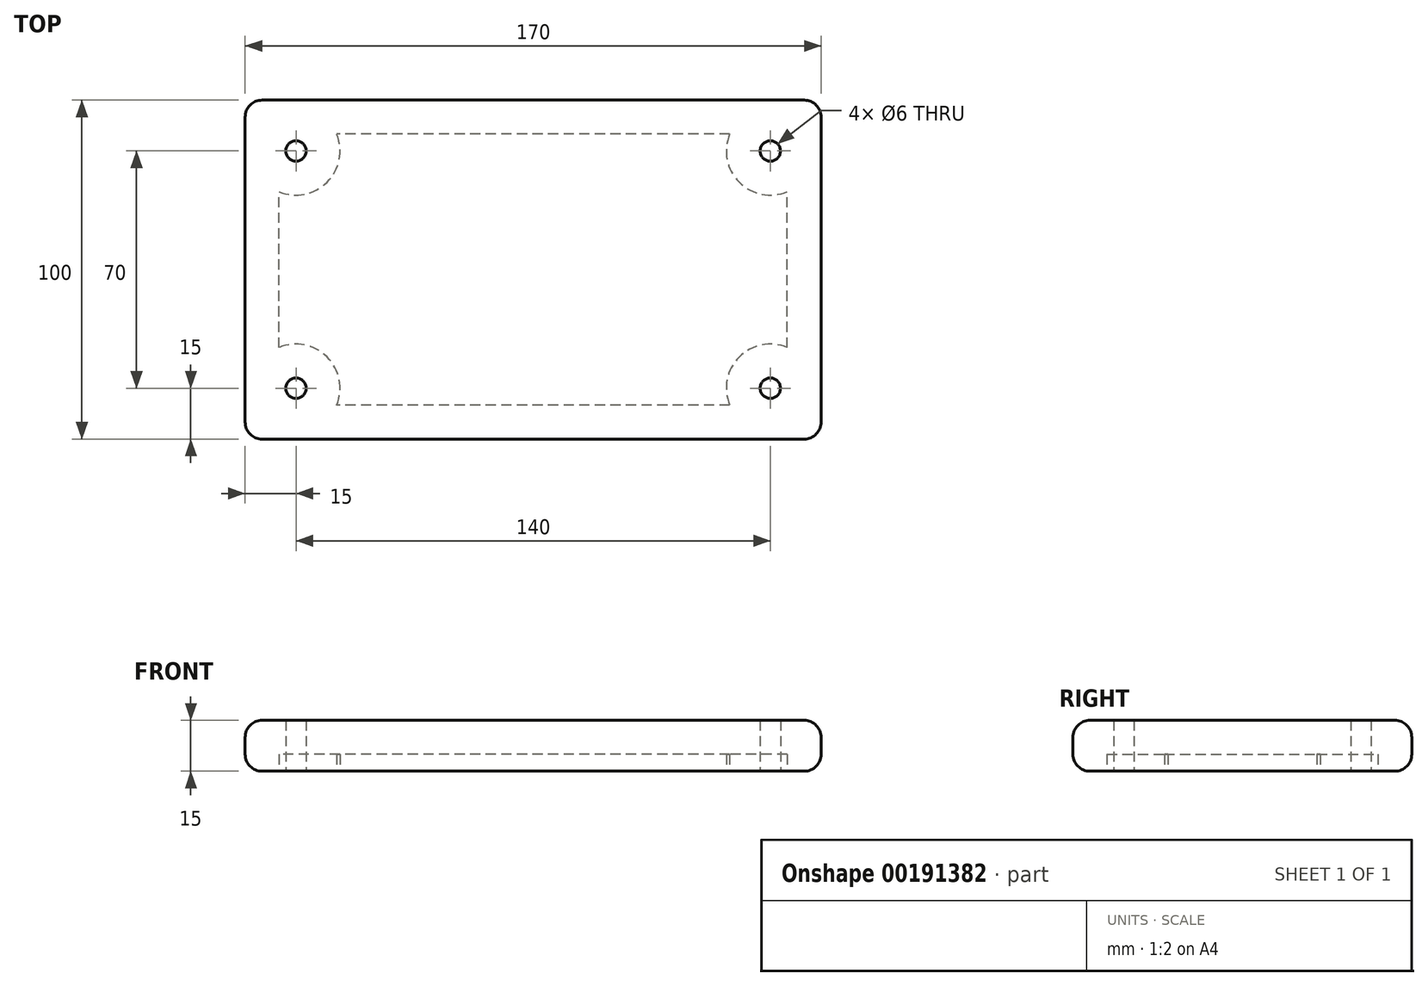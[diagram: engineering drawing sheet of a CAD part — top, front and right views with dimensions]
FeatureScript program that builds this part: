
annotation { "Feature Type Name" : "Feature", "Feature Type Description" : "" }
export const myFeature = defineFeature(function(context is Context, id is Id, definition is map)
    precondition{}
    {
        {
            var Q0;
            Q0=qCreatedBy(makeId("Top.planeOp"),FACE);
            var sketch = newSketch(context, id + "F0", { "sketchPlane" : qUnion([Q0])});
            skLineSegment(sketch, "E0.bottom", {"start": v(85, -50) * mm, "end": v(-85, -50) * mm});
            skLineSegment(sketch, "E0.top", {"start": v(85, 50) * mm, "end": v(-85, 50) * mm});
            skLineSegment(sketch, "E0.left", {"start": v(85, -50) * mm, "end": v(85, 50) * mm});
            skLineSegment(sketch, "E0.right", {"start": v(-85, -50) * mm, "end": v(-85, 50) * mm});
            skPoint(sketch, "E0.middle", {"position": v(0, 0) * mm});
            skCircle(sketch, "E1", {"center": v(-70, -35) * mm, "radius": 3 * mm});
            skCircle(sketch, "E2", {"center": v(-70, 35) * mm, "radius": 3 * mm});
            skCircle(sketch, "E3", {"center": v(70, -35) * mm, "radius": 3 * mm});
            skCircle(sketch, "E4", {"center": v(70, 35) * mm, "radius": 3 * mm});
            skSolve(sketch);
        }
        {
            var Q0;
            Q0=makeQuery(id+"F0.imprint","IMPRINT",FACE,{"disambiguationData":[TD([[makeQuery(id+"F0.imprint","IMPRINT",EDGE,{"derivedFrom":sQuery(id+"F0.wireOp",EDGE,"E0.bottom")}),-1.0]])]});
            extrude(context, id + "F1", {"entities" : qUnion([Q0]), "endBound" : BoundingType.SYMMETRIC, "depth" : 15 * mm});
        }
        {
            var Q0;
            Q0=makeQuery(id+"F1.opExtrude","CAP_FACE",FACE,{"disambiguationData":[OSD([sQuery(id+"F0.wireOp",EDGE,"E0.bottom"),sQuery(id+"F0.wireOp",EDGE,"E0.top"),sQuery(id+"F0.wireOp",EDGE,"E0.left"),sQuery(id+"F0.wireOp",EDGE,"E0.right")])],"isStart":true});
            shell(context, id + "F2", {"entities" : qUnion([Q0]), "thickness" : 10 * mm});
        }
        {
            var Q0;
            Q0=makeQuery(id+"F1.opExtrude","CAP_EDGE",EDGE,{"disambiguationData":[OSD([sQuery(id+"F0.wireOp",EDGE,"E0.right")])],"isStart":true});
            var Q1;
            Q1=makeQuery(id+"F1.opExtrude","CAP_EDGE",EDGE,{"disambiguationData":[OSD([sQuery(id+"F0.wireOp",EDGE,"E0.right")])],"isStart":false});
            var Q2;
            Q2=makeQuery(id+"F1.opExtrude","CAP_EDGE",EDGE,{"disambiguationData":[OSD([sQuery(id+"F0.wireOp",EDGE,"E0.bottom")])],"isStart":false});
            var Q3;
            Q3=makeQuery(id+"F1.opExtrude","CAP_EDGE",EDGE,{"disambiguationData":[OSD([sQuery(id+"F0.wireOp",EDGE,"E0.bottom")])],"isStart":true});
            var Q4;
            Q4=makeQuery(id+"F1.opExtrude","CAP_EDGE",EDGE,{"disambiguationData":[OSD([sQuery(id+"F0.wireOp",EDGE,"E0.left")])],"isStart":true});
            var Q5;
            Q5=makeQuery(id+"F1.opExtrude","CAP_EDGE",EDGE,{"disambiguationData":[OSD([sQuery(id+"F0.wireOp",EDGE,"E0.left")])],"isStart":false});
            var Q6;
            Q6=makeQuery(id+"F1.opExtrude","SWEPT_EDGE",EDGE,{"disambiguationData":[OSD([sQuery(id+"F0.wireOp",EDGE,"E0.top"),sQuery(id+"F0.wireOp",EDGE,"E0.left")])]});
            var Q7;
            Q7=makeQuery(id+"F1.opExtrude","CAP_EDGE",EDGE,{"disambiguationData":[OSD([sQuery(id+"F0.wireOp",EDGE,"E0.top")])],"isStart":false});
            var Q8;
            Q8=makeQuery(id+"F1.opExtrude","CAP_EDGE",EDGE,{"disambiguationData":[OSD([sQuery(id+"F0.wireOp",EDGE,"E0.top")])],"isStart":true});
            var Q9;
            Q9=makeQuery(id+"F1.opExtrude","SWEPT_EDGE",EDGE,{"disambiguationData":[OSD([sQuery(id+"F0.wireOp",EDGE,"E0.top"),sQuery(id+"F0.wireOp",EDGE,"E0.right")])]});
            var Q10;
            Q10=makeQuery(id+"F1.opExtrude","SWEPT_EDGE",EDGE,{"disambiguationData":[OSD([sQuery(id+"F0.wireOp",EDGE,"E0.bottom"),sQuery(id+"F0.wireOp",EDGE,"E0.right")])]});
            var Q11;
            Q11=makeQuery(id+"F1.opExtrude","SWEPT_EDGE",EDGE,{"disambiguationData":[OSD([sQuery(id+"F0.wireOp",EDGE,"E0.bottom"),sQuery(id+"F0.wireOp",EDGE,"E0.left")])]});
            fillet(context, id + "F3", {"entities" : qUnion([Q0, Q1, Q2, Q3, Q4, Q5, Q6, Q7, Q8, Q9, Q10, Q11]), "radius" : 5 * mm, "tangentPropagation" : true, "allowEdgeOverflow" : false});
        }
        {
            var Q0;
            Q0=makeQuery(id+"F2.opShell","OFFSET_FACE",FACE,{"disambiguationData":[OSD([sQuery(id+"F0.wireOp",EDGE,"E0.bottom"),sQuery(id+"F0.wireOp",EDGE,"E0.top"),sQuery(id+"F0.wireOp",EDGE,"E0.left"),sQuery(id+"F0.wireOp",EDGE,"E0.right")])]});
            var sketch = newSketch(context, id + "F4", { "sketchPlane" : qUnion([Q0])});
            skLineSegment(sketch, "E5.bottom", {"start": v(75, -40) * mm, "end": v(65, -40) * mm});
            skLineSegment(sketch, "E5.left", {"start": v(75, -40) * mm, "end": v(75, -30) * mm});
            skLineSegment(sketch, "E6.bottom", {"start": v(-75, -40) * mm, "end": v(-65, -40) * mm});
            skLineSegment(sketch, "E6.left", {"start": v(-75, -40) * mm, "end": v(-75, -30) * mm});
            skLineSegment(sketch, "E7.bottom", {"start": v(-75, 40) * mm, "end": v(-65, 40) * mm});
            skLineSegment(sketch, "E7.left", {"start": v(-75, 40) * mm, "end": v(-75, 30) * mm});
            skLineSegment(sketch, "E8.bottom", {"start": v(75, 40) * mm, "end": v(65, 40) * mm});
            skLineSegment(sketch, "E8.left", {"start": v(75, 40) * mm, "end": v(75, 30) * mm});
            skArc(sketch, "E9", {"start": v(75, -30) * mm, "mid": v(65, -30) * mm, "end": v(65, -40) * mm});
            skArc(sketch, "E10", {"start": v(65, 40) * mm, "mid": v(65, 30) * mm, "end": v(75, 30) * mm});
            skArc(sketch, "E11", {"start": v(-65, -40) * mm, "mid": v(-65, -30) * mm, "end": v(-75, -30) * mm});
            skArc(sketch, "E12", {"start": v(-75, 30) * mm, "mid": v(-65, 30) * mm, "end": v(-65, 40) * mm});
            skCircle(sketch, "E13", {"center": v(70, 35) * mm, "radius": 3 * mm});
            skCircle(sketch, "E14", {"center": v(-70, 35) * mm, "radius": 3 * mm});
            skCircle(sketch, "E15", {"center": v(-70, -35) * mm, "radius": 3 * mm});
            skCircle(sketch, "E16", {"center": v(70, -35) * mm, "radius": 3 * mm});
            skSolve(sketch);
        }
        {
            var Q0;
            Q0 = qSketchRegion(id + "F4", true);
            extrude(context, id + "F5", {"entities" : qUnion([Q0]), "operationType" : NewBodyOperationType.ADD, "depth" : 5 * mm});
        }
    });
